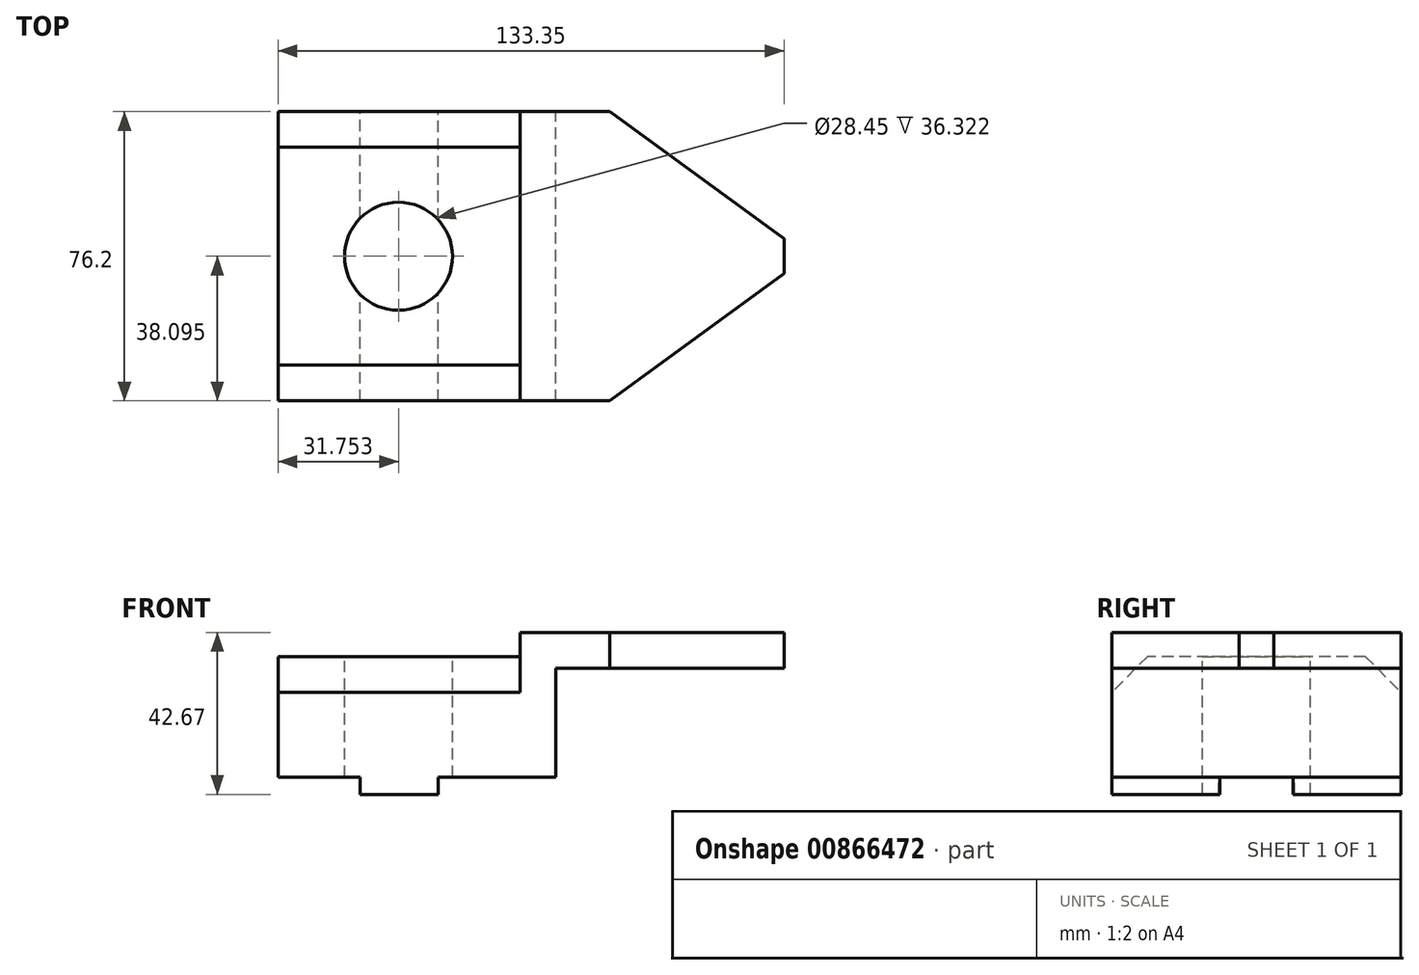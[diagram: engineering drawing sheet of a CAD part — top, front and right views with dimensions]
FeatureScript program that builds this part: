
annotation { "Feature Type Name" : "Feature", "Feature Type Description" : "" }
export const myFeature = defineFeature(function(context is Context, id is Id, definition is map)
    precondition{}
    {
        {
            var Q0;
            Q0=qCreatedBy(makeId("Top.planeOp"),FACE);
            var sketch = newSketch(context, id + "F0", { "sketchPlane" : qUnion([Q0])});
            skLineSegment(sketch, "E0", {"start": v(-52.9, 27.6) * mm, "end": v(-52.9, -10.5) * mm});
            skLineSegment(sketch, "E1", {"start": v(-52.9, -10.5) * mm, "end": v(20.25, -10.5) * mm});
            skLineSegment(sketch, "E2", {"start": v(20.25, -10.5) * mm, "end": v(20.25, 27.6) * mm});
            skLineSegment(sketch, "E3", {"start": v(20.25, 27.6) * mm, "end": v(-52.9, 27.6) * mm});
            skLineSegment(sketch, "E4", {"start": v(-31.32, -10.5) * mm, "end": v(-31.32, 27.6) * mm});
            skLineSegment(sketch, "E5", {"start": v(-10.74, -10.5) * mm, "end": v(-10.74, 27.6) * mm});
            skSolve(sketch);
        }
        {
            var Q0;
            {var subQ0=sQuery(id+"F0.wireOp",EDGE,"E4");Q0=makeQuery(id+"F0.imprint","IMPRINT",FACE,{"disambiguationData":[TD([[makeQuery(id+"F0.imprint","IMPRINT",EDGE,{"derivedFrom":subQ0}),-1.0]])]});}
            extrude(context, id + "F1", {"entities" : qUnion([Q0]), "oppositeDirection" : true, "depth" : 4.57 * mm, "offsetDistance" : 25.4 * mm});
        }
        {
            var Q0;
            {var subQ0=sQuery(id+"F0.wireOp",EDGE,"E0");Q0=makeQuery(id+"F0.imprint","IMPRINT",FACE,{"disambiguationData":[TD([[makeQuery(id+"F0.imprint","IMPRINT",EDGE,{"derivedFrom":subQ0}),1.0]])]});}
            var Q1;
            {var subQ0=sQuery(id+"F0.wireOp",EDGE,"E2");Q1=makeQuery(id+"F0.imprint","IMPRINT",FACE,{"disambiguationData":[TD([[makeQuery(id+"F0.imprint","IMPRINT",EDGE,{"derivedFrom":subQ0}),1.0]])]});}
            var Q2;
            {var subQ0=sQuery(id+"F0.wireOp",EDGE,"E4");Q2=makeQuery(id+"F0.imprint","IMPRINT",FACE,{"disambiguationData":[TD([[makeQuery(id+"F0.imprint","IMPRINT",EDGE,{"derivedFrom":subQ0}),-1.0]])]});}
            extrude(context, id + "F2", {"entities" : qUnion([Q0, Q1, Q2]), "operationType" : NewBodyOperationType.ADD, "depth" : 38.1 * mm, "offsetDistance" : 25.4 * mm});
        }
        {
            var Q0;
            Q0=makeQuery(id+"F2.opExtrude","SWEPT_FACE",FACE,{"disambiguationData":[OSD([sQuery(id+"F0.wireOp",EDGE,"E0")])]});
            var sketch = newSketch(context, id + "F3", { "sketchPlane" : qUnion([Q0])});
            skLineSegment(sketch, "E6", {"start": v(-27.6, 31.75) * mm, "end": v(1.1, 31.75) * mm});
            skLineSegment(sketch, "E7", {"start": v(1.1, 31.75) * mm, "end": v(10.5, 22.35) * mm});
            skSolve(sketch);
        }
        {
            var Q0;
            Q0=makeQuery(id+"F2.opExtrude","CAP_FACE",FACE,{"disambiguationData":[OSD([sQuery(id+"F0.wireOp",EDGE,"E0"),sQuery(id+"F0.wireOp",EDGE,"E1"),sQuery(id+"F0.wireOp",EDGE,"E2"),sQuery(id+"F0.wireOp",EDGE,"E3")])],"isStart":false});
            var sketch = newSketch(context, id + "F4", { "sketchPlane" : qUnion([Q0])});
            skLineSegment(sketch, "E8", {"start": v(10.85, -10.5) * mm, "end": v(34.47, -10.5) * mm});
            skLineSegment(sketch, "E9", {"start": v(34.47, -10.5) * mm, "end": v(80.44, 23.03) * mm});
            skLineSegment(sketch, "E10", {"start": v(80.44, 23.03) * mm, "end": v(80.44, 27.6) * mm});
            skLineSegment(sketch, "E11", {"start": v(80.44, 27.6) * mm, "end": v(10.85, 27.6) * mm});
            skLineSegment(sketch, "E12", {"start": v(10.85, 27.6) * mm, "end": v(10.85, -10.5) * mm});
            skSolve(sketch);
        }
        {
            var Q0;
            {var subQ3=sQuery(id+"F4.wireOp",EDGE,"E9");Q0=makeQuery(id+"F4.imprint","IMPRINT",FACE,{"disambiguationData":[TD([[makeQuery(id+"F4.imprint","IMPRINT",EDGE,{"derivedFrom":subQ3}),1.0]])]});}
            var Q1;
            {var subQ2=sQuery(id+"F4.wireOp",EDGE,"E12");Q1=makeQuery(id+"F4.imprint","IMPRINT",FACE,{"disambiguationData":[TD([[makeQuery(id+"F4.imprint","IMPRINT",EDGE,{"derivedFrom":subQ2}),1.0]])]});}
            extrude(context, id + "F5", {"entities" : qUnion([Q0, Q1]), "operationType" : NewBodyOperationType.ADD, "oppositeDirection" : true, "depth" : 9.4 * mm, "offsetDistance" : 25.4 * mm});
        }
        {
            var Q0;
            {var subQ4=sQuery(id+"F3.wireOp",EDGE,"E6");Q0=makeQuery(id+"F3.imprint","IMPRINT",FACE,{"disambiguationData":[TD([[makeQuery(id+"F3.imprint","IMPRINT",EDGE,{"derivedFrom":subQ4}),1.0]])]});}
            extrude(context, id + "F6", {"entities" : qUnion([Q0]), "operationType" : NewBodyOperationType.REMOVE, "oppositeDirection" : true, "depth" : 63.75 * mm, "offsetDistance" : 25.4 * mm});
        }
        {
            var Q0;
            Q0=makeQuery(id+"F1.opExtrude","SWEPT_BODY",BODY,{"disambiguationData":[OSD([sQuery(id+"F0.wireOp",EDGE,"E1"),sQuery(id+"F0.wireOp",EDGE,"E3"),sQuery(id+"F0.wireOp",EDGE,"E4"),sQuery(id+"F0.wireOp",EDGE,"E5")])]});
            var Q1;
            {var subQ0=sQuery(id+"F0.wireOp",EDGE,"E3");Q1=makeQuery(id+"F5.boolean.opBoolean","MERGE",FACE,{"derivedFrom":[makeQuery(id+"F2.boolean.opBoolean","MERGE",FACE,{"derivedFrom":[makeQuery(id+"F1.opExtrude","SWEPT_FACE",FACE,{"disambiguationData":[OSD([subQ0])]}),makeQuery(id+"F2.opExtrude","SWEPT_FACE",FACE,{"disambiguationData":[OSD([subQ0])]})]}),makeQuery(id+"F5.opExtrude","SWEPT_FACE",FACE,{"disambiguationData":[OSD([sQuery(id+"F4.wireOp",EDGE,"E11")])]})]});}
            mirror(context, id + "F7", {"operationType" : NewBodyOperationType.ADD, "entities" : qUnion([Q0]), "mirrorPlane" : qUnion([Q1])});
        }
        {
            var Q0;
            {var subQ0=makeQuery(id+"F6.boolean.opBoolean","COPY",FACE,{"derivedFrom":makeQuery(id+"F6.opExtrude","SWEPT_FACE",FACE,{"disambiguationData":[OSD([sQuery(id+"F3.wireOp",EDGE,"E6")])]})});Q0=makeQuery(id+"F7.boolean.opBoolean","MERGE",FACE,{"derivedFrom":[subQ0,makeQuery(id+"F7.opPattern","COPY",FACE,{"derivedFrom":subQ0,"instanceName":"1"})]});}
            var sketch = newSketch(context, id + "F8", { "sketchPlane" : qUnion([Q0])});
            skCircle(sketch, "E13", {"center": v(-21.16, 27.6) * mm, "radius": 14.22 * mm});
            skPoint(sketch, "E13.centerSnap0", {"position": v(-52.9, 27.6) * mm});
            skSolve(sketch);
        }
        {
            var Q0;
            Q0 = qSketchRegion(id + "F8", true);
            extrude(context, id + "F9", {"entities" : qUnion([Q0]), "operationType" : NewBodyOperationType.REMOVE, "endBound" : BoundingType.UP_TO_NEXT, "oppositeDirection" : true, "depth" : 25.4 * mm, "offsetDistance" : 25.4 * mm});
        }
    });
